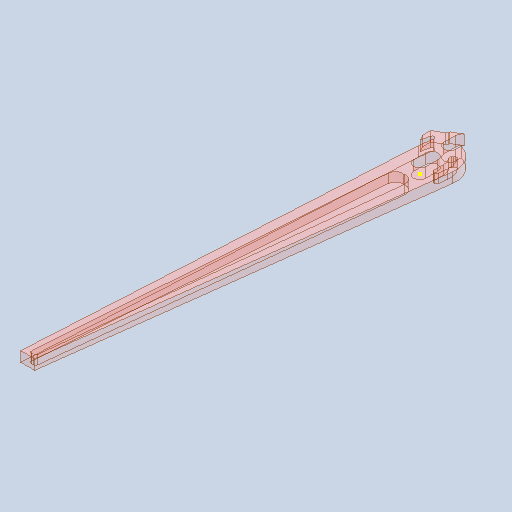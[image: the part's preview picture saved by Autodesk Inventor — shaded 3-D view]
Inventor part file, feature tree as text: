
AUTODESK INVENTOR PART (.ipt)
format: ipt  version: 2023 (Build 270158000, 158)  size: 634,368 bytes
history: native  units: mm
features: sketch x22, extrude x17, fillet x11, other x9, projected_geometry x8
ambient origin geometry x8: Origin, YZ Plane, XZ Plane, XY Plane, X Axis, Y Axis, Z Axis, Center Point
bodies: Body1 (feature_tree)
feature tree (67):
  other  "ソリッド1"
  sketch  "スケッチ1"
  extrude  "押し出し1"  Depth=6.0mm
  extrude  "押し出し2"  Depth=6.0mm
  sketch  "スケッチ4"
  fillet  "フィレット1"  Radius=3.0mm
  fillet  "フィレット2"  Radius=3.0mm
  fillet  "フィレット3"  Radius=6.0mm
  fillet  "フィレット4"  Radius=6.0mm
  extrude  "押し出し3"  Depth=6.0mm
  fillet  "フィレット5"  Radius=3.0mm
  sketch  "スケッチ6"
  extrude  "押し出し4"  Depth=7.0mm
  sketch  "スケッチ8"
  extrude  "押し出し5"  Depth=160.0mm
  extrude  "押し出し6"  Depth=15.0mm
  extrude  "押し出し7"  Depth=3.0mm
  fillet  "フィレット6"  Radius=5.0mm
  fillet  "フィレット7"  Radius=5.0mm
  extrude  "押し出し8"  Depth=5.0mm
  fillet  "フィレット8"  Radius=4.0mm
  sketch  "スケッチ11"
  sketch  "スケッチ12"
  extrude  "押し出し9"  Depth=4.0mm TaperAngle=0.0deg
  sketch  "スケッチ14"
  extrude  "押し出し10"  Depth=3.0mm
  extrude  "押し出し11"  Depth=4.0mm
  sketch  "スケッチ15"
  extrude  "押し出し12"  Depth=2.0mm
  sketch  "スケッチ17"
  extrude  "押し出し13"  Depth=1.0mm
  extrude  "押し出し14"  Depth=3.0mm
  sketch  "スケッチ20"
  sketch  "スケッチ21"
  extrude  "押し出し15"  Depth=8.0mm
  extrude  "押し出し16"  Depth=1.0mm
  fillet  "フィレット9"  Radius=5.0mm
  fillet  "フィレット10"  Radius=4.0mm
  extrude  "押し出し17"  Depth=3.0mm
  fillet  "フィレット11"  Radius=4.5mm
  sketch  "スケッチ2"
  sketch  "スケッチ3"
  sketch  "スケッチ5"
  sketch  "スケッチ7"
  sketch  "スケッチ9"
  sketch  "スケッチ10"
  projected_geometry  "投影ループ1"
  projected_geometry  "投影ループ2"
  sketch  "スケッチ13"
  projected_geometry  "投影ループ3"
  sketch  "スケッチ16"
  sketch  "スケッチ18"
  projected_geometry  "投影ループ4"
  sketch  "スケッチ19"
  projected_geometry  "投影ループ5"
  projected_geometry  "投影ループ6"
  projected_geometry  "投影ループ7"
  sketch  "スケッチ22"
  projected_geometry  "投影ループ8"
  other  "断面エッジを投影1"
  other  "断面エッジを投影2"
  other  "断面エッジを投影3"
  other  "断面エッジを投影4"
  other  "断面エッジを投影5"
  other  "断面エッジを投影6"
  other  "断面エッジを投影7"
  other  "断面エッジを投影8"
